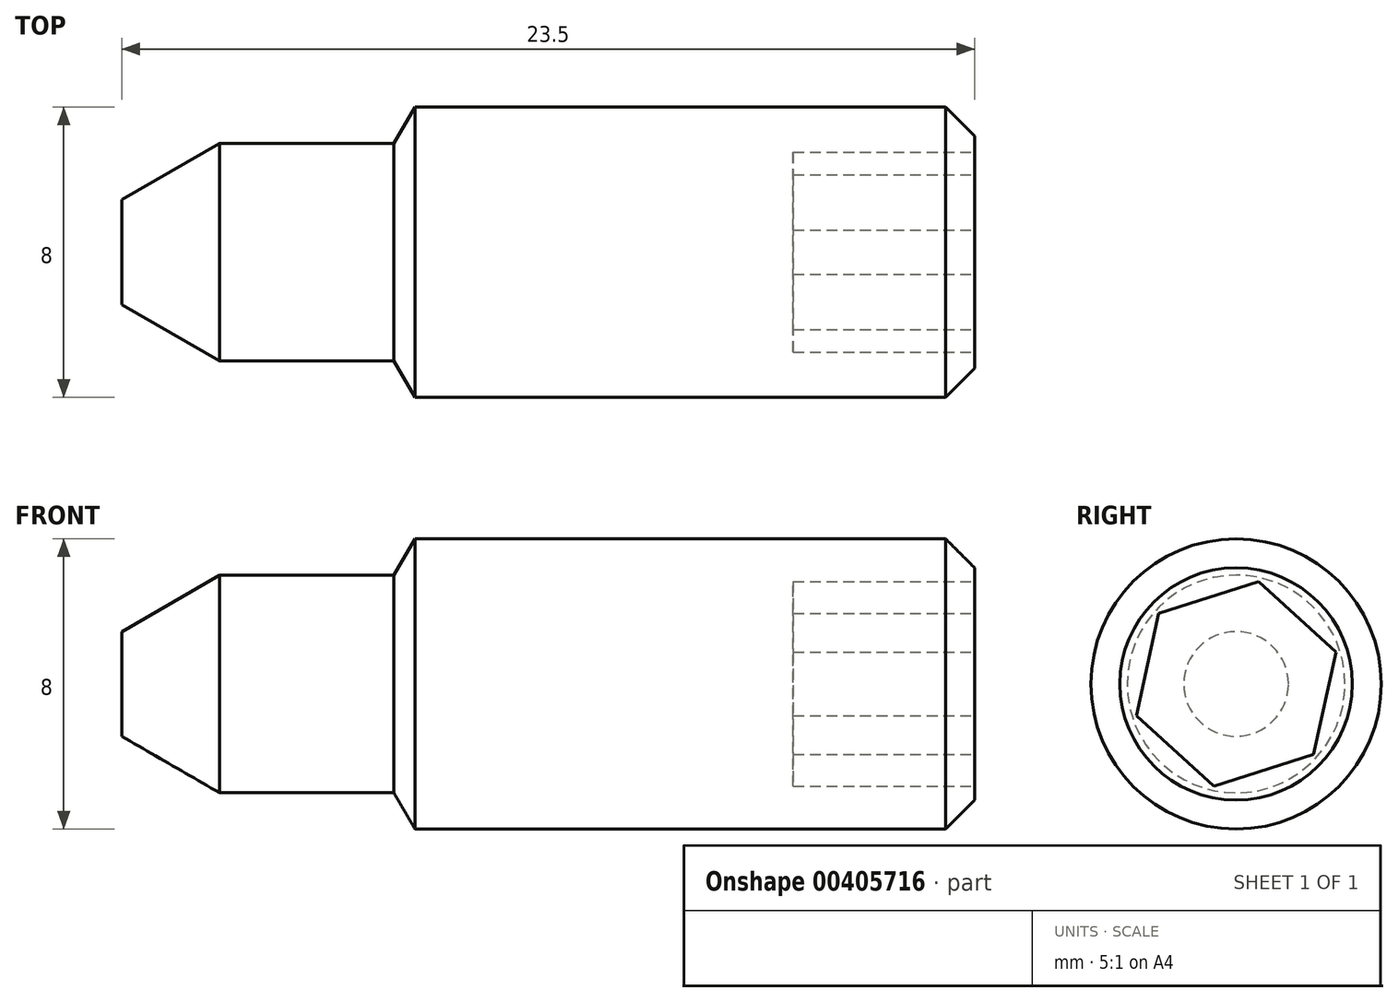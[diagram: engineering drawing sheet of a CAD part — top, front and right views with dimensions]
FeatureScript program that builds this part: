
annotation { "Feature Type Name" : "Feature", "Feature Type Description" : "" }
export const myFeature = defineFeature(function(context is Context, id is Id, definition is map)
    precondition{}
    {
        {
            var Q0;
            Q0=qCreatedBy(makeId("Front.planeOp"),FACE);
            var sketch = newSketch(context, id + "F0", { "sketchPlane" : qUnion([Q0])});
            skLineSegment(sketch, "E0", {"start": v(37.44, -118.42) * mm, "end": v(37.44, -124.3) * mm, "construction": true});
            skLineSegment(sketch, "E1", {"start": v(39.94, -122.86) * mm, "end": v(42.63, -121.3) * mm});
            skLineSegment(sketch, "E2", {"start": v(42.63, -121.3) * mm, "end": v(47.44, -121.3) * mm});
            skLineSegment(sketch, "E3", {"start": v(47.44, -121.3) * mm, "end": v(48.01, -120.3) * mm});
            skLineSegment(sketch, "E4", {"start": v(48.01, -120.3) * mm, "end": v(63.44, -120.3) * mm});
            skLineSegment(sketch, "E5", {"start": v(63.44, -120.3) * mm, "end": v(63.44, -124.3) * mm});
            skLineSegment(sketch, "E6", {"start": v(63.44, -124.3) * mm, "end": v(39.94, -124.3) * mm});
            skLineSegment(sketch, "E7", {"start": v(37.44, -124.3) * mm, "end": v(25.77, -114.7) * mm, "construction": true});
            skLineSegment(sketch, "E8", {"start": v(37.44, -124.3) * mm, "end": v(22.74, -124.3) * mm, "construction": true});
            skLineSegment(sketch, "E9.0", {"start": v(39.94, -122.86) * mm, "end": v(39.94, -124.3) * mm});
            skPoint(sketch, "E10.orphan", {"position": v(40.04, -122.8) * mm});
            skSolve(sketch);
        }
        {
            var Q0;
            Q0=makeQuery(id+"F0.imprint","IMPRINT",FACE,{"disambiguationData":[TD([[makeQuery(id+"F0.imprint","IMPRINT",EDGE,{"derivedFrom":sQuery(id+"F0.wireOp",EDGE,"E1")}),-1.0]])]});
            var Q1;
            Q1=sQuery(id+"F0.wireOp",EDGE,"E6");
            revolve(context, id + "F1", {"entities" : qUnion([Q0]), "axis" : qUnion([Q1]), "revolveType" : RevolveType.FULL});
        }
        {
            var Q0;
            Q0=makeQuery(id+"F1.opRevolve","SWEPT_FACE",FACE,{"disambiguationData":[OSD([sQuery(id+"F0.wireOp",EDGE,"E5")])]});
            var sketch = newSketch(context, id + "F2", { "sketchPlane" : qUnion([Q0])});
            skCircle(sketch, "E11.0", {"center": v(0, -124.3) * mm, "radius": 4 * mm});
            skCircle(sketch, "E12.cCircle", {"center": v(0, -124.3) * mm, "radius": 2.89 * mm, "construction": true});
            skLineSegment(sketch, "E12.0", {"start": v(0.61, -121.48) * mm, "end": v(2.75, -123.42) * mm});
            skLineSegment(sketch, "E12.1", {"start": v(2.75, -123.42) * mm, "end": v(2.14, -126.24) * mm});
            skLineSegment(sketch, "E12.2", {"start": v(2.14, -126.24) * mm, "end": v(-0.61, -127.12) * mm});
            skLineSegment(sketch, "E12.3", {"start": v(-0.61, -127.12) * mm, "end": v(-2.75, -125.18) * mm});
            skLineSegment(sketch, "E12.4", {"start": v(-2.75, -125.18) * mm, "end": v(-2.14, -122.36) * mm});
            skLineSegment(sketch, "E12.5", {"start": v(-2.14, -122.36) * mm, "end": v(0.61, -121.48) * mm});
            skSolve(sketch);
        }
        {
            var Q0;
            Q0=makeQuery(id+"F2.imprint","IMPRINT",FACE,{"disambiguationData":[TD([[makeQuery(id+"F2.imprint","IMPRINT",EDGE,{"derivedFrom":sQuery(id+"F2.wireOp",EDGE,"E12.0")}),-1.0]])]});
            extrude(context, id + "F3", {"entities" : qUnion([Q0]), "operationType" : NewBodyOperationType.REMOVE, "oppositeDirection" : true, "depth" : 5 * mm});
        }
        {
            var Q0;
            Q0=makeQuery(id+"F1.opRevolve","SWEPT_EDGE",EDGE,{"disambiguationData":[OSD([sQuery(id+"F0.wireOp",EDGE,"E4"),sQuery(id+"F0.wireOp",EDGE,"E5")])]});
            chamfer(context, id + "F4", {"entities" : qUnion([Q0]), "width" : 0.8 * mm, "tangentPropagation" : true});
        }
    });
